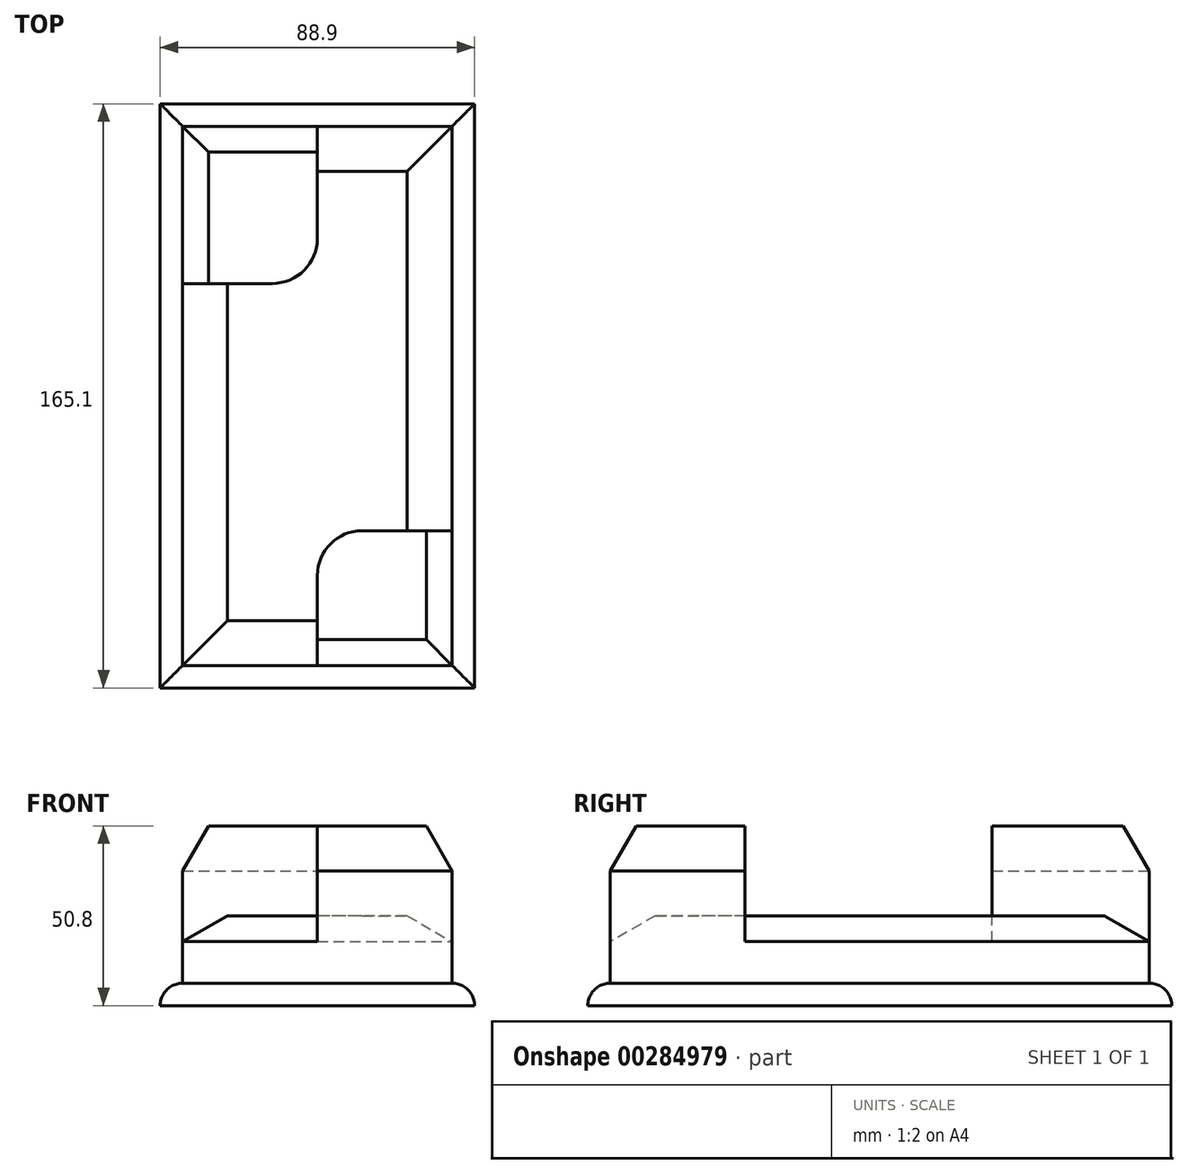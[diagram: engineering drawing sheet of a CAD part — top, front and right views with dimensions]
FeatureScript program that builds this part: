
annotation { "Feature Type Name" : "Feature", "Feature Type Description" : "" }
export const myFeature = defineFeature(function(context is Context, id is Id, definition is map)
    precondition{}
    {
        {
            var Q0;
            Q0=qCreatedBy(makeId("Top.planeOp"),FACE);
            var sketch = newSketch(context, id + "F0", { "sketchPlane" : qUnion([Q0])});
            skLineSegment(sketch, "E0.bottom", {"start": v(-67.89, 79.36) * mm, "end": v(21.01, 79.36) * mm});
            skLineSegment(sketch, "E0.top", {"start": v(-67.89, -85.74) * mm, "end": v(21.01, -85.74) * mm});
            skLineSegment(sketch, "E0.left", {"start": v(-67.89, 79.36) * mm, "end": v(-67.89, -85.74) * mm});
            skLineSegment(sketch, "E0.right", {"start": v(21.01, 79.36) * mm, "end": v(21.01, -85.74) * mm});
            skLineSegment(sketch, "E1.bottom", {"start": v(-61.54, 73) * mm, "end": v(14.66, 73) * mm});
            skLineSegment(sketch, "E1.top", {"start": v(-61.54, -79.4) * mm, "end": v(14.66, -79.4) * mm});
            skLineSegment(sketch, "E1.left", {"start": v(-61.54, 73) * mm, "end": v(-61.54, -79.4) * mm});
            skLineSegment(sketch, "E1.right", {"start": v(14.66, 73) * mm, "end": v(14.66, -79.4) * mm});
            skLineSegment(sketch, "E2", {"start": v(-23.44, -79.4) * mm, "end": v(-23.44, -54) * mm});
            skLineSegment(sketch, "E3", {"start": v(-10.74, -41.3) * mm, "end": v(14.66, -41.3) * mm});
            skPoint(sketch, "E4.visualSharp", {"position": v(-23.44, -41.3) * mm});
            skArc(sketch, "E4.filletArc", {"start": v(-10.74, -41.3) * mm, "mid": v(-19.72, -45.01) * mm, "end": v(-23.44, -54) * mm});
            skLineSegment(sketch, "E5", {"start": v(-61.54, 28.56) * mm, "end": v(-36.14, 28.56) * mm});
            skLineSegment(sketch, "E6", {"start": v(-23.44, 41.26) * mm, "end": v(-23.44, 73) * mm});
            skPoint(sketch, "E7.visualSharp", {"position": v(-23.44, 28.56) * mm});
            skArc(sketch, "E7.filletArc", {"start": v(-36.14, 28.56) * mm, "mid": v(-27.16, 32.28) * mm, "end": v(-23.44, 41.26) * mm});
            skSolve(sketch);
        }
        {
            var Q0;
            Q0=makeQuery(id+"F0.imprint","IMPRINT",FACE,{"disambiguationData":[TD([[makeQuery(id+"F0.imprint","IMPRINT",EDGE,{"derivedFrom":sQuery(id+"F0.wireOp",EDGE,"E0.bottom")}),-1.0]])]});
            extrude(context, id + "F1", {"entities" : qUnion([Q0]), "depth" : 6.35 * mm});
        }
        {
            var Q0;
            {var subQ4=sQuery(id+"F0.wireOp",EDGE,"E2");Q0=makeQuery(id+"F0.imprint","IMPRINT",FACE,{"disambiguationData":[TD([[makeQuery(id+"F0.imprint","IMPRINT",EDGE,{"derivedFrom":subQ4}),1.0]])]});}
            extrude(context, id + "F2", {"entities" : qUnion([Q0]), "operationType" : NewBodyOperationType.ADD, "depth" : 25.4 * mm});
        }
        {
            var Q0;
            {var subQ1=sQuery(id+"F0.wireOp",EDGE,"E5");Q0=makeQuery(id+"F0.imprint","IMPRINT",FACE,{"disambiguationData":[TD([[makeQuery(id+"F0.imprint","IMPRINT",EDGE,{"derivedFrom":subQ1}),1.0]])]});}
            var Q1;
            {var subQ4=sQuery(id+"F0.wireOp",EDGE,"E2");Q1=makeQuery(id+"F0.imprint","IMPRINT",FACE,{"disambiguationData":[TD([[makeQuery(id+"F0.imprint","IMPRINT",EDGE,{"derivedFrom":subQ4}),-1.0]])]});}
            extrude(context, id + "F3", {"entities" : qUnion([Q0, Q1]), "operationType" : NewBodyOperationType.ADD, "depth" : 50.8 * mm});
        }
        {
            var Q0;
            Q0=makeQuery(id+"F1.opExtrude","CAP_EDGE",EDGE,{"disambiguationData":[OSD([sQuery(id+"F0.wireOp",EDGE,"E0.bottom")])],"isStart":false});
            var Q1;
            Q1=makeQuery(id+"F1.opExtrude","CAP_EDGE",EDGE,{"disambiguationData":[OSD([sQuery(id+"F0.wireOp",EDGE,"E0.left")])],"isStart":false});
            var Q2;
            Q2=makeQuery(id+"F1.opExtrude","CAP_EDGE",EDGE,{"disambiguationData":[OSD([sQuery(id+"F0.wireOp",EDGE,"E0.top")])],"isStart":false});
            var Q3;
            Q3=makeQuery(id+"F1.opExtrude","CAP_EDGE",EDGE,{"disambiguationData":[OSD([sQuery(id+"F0.wireOp",EDGE,"E0.right")])],"isStart":false});
            fillet(context, id + "F4", {"entities" : qUnion([Q0, Q1, Q2, Q3]), "radius" : 6.35 * mm, "tangentPropagation" : true, "allowEdgeOverflow" : false});
        }
        {
            var Q0;
            Q0=makeQuery(id+"F2.opExtrude","CAP_EDGE",EDGE,{"disambiguationData":[OSD([sQuery(id+"F0.wireOp",EDGE,"E1.left")])],"isStart":false});
            var Q1;
            Q1=makeQuery(id+"F2.opExtrude","CAP_EDGE",EDGE,{"disambiguationData":[OSD([sQuery(id+"F0.wireOp",EDGE,"E1.bottom")])],"isStart":false});
            var Q2;
            Q2=makeQuery(id+"F2.opExtrude","CAP_EDGE",EDGE,{"disambiguationData":[OSD([sQuery(id+"F0.wireOp",EDGE,"E1.right")])],"isStart":false});
            var Q3;
            Q3=makeQuery(id+"F2.opExtrude","CAP_EDGE",EDGE,{"disambiguationData":[OSD([sQuery(id+"F0.wireOp",EDGE,"E1.top")])],"isStart":false});
            chamfer(context, id + "F5", {"entities" : qUnion([Q0, Q1, Q2, Q3]), "chamferType" : ChamferType.OFFSET_ANGLE, "width" : 12.7 * mm, "oppositeDirection" : false, "angle" : 30 * degree, "tangentPropagation" : true});
        }
        {
            var Q0;
            Q0=makeQuery(id+"F3.opExtrude","CAP_EDGE",EDGE,{"disambiguationData":[OSD([sQuery(id+"F0.wireOp",EDGE,"E1.bottom")])],"isStart":false});
            var Q1;
            Q1=makeQuery(id+"F3.opExtrude","CAP_EDGE",EDGE,{"disambiguationData":[OSD([sQuery(id+"F0.wireOp",EDGE,"E1.left")])],"isStart":false});
            chamfer(context, id + "F6", {"entities" : qUnion([Q0, Q1]), "chamferType" : ChamferType.OFFSET_ANGLE, "width" : 12.7 * mm, "oppositeDirection" : false, "angle" : 30 * degree, "tangentPropagation" : true});
        }
        {
            var Q0;
            Q0=makeQuery(id+"F3.opExtrude","CAP_EDGE",EDGE,{"disambiguationData":[OSD([sQuery(id+"F0.wireOp",EDGE,"E1.right")])],"isStart":false});
            var Q1;
            Q1=makeQuery(id+"F3.opExtrude","CAP_EDGE",EDGE,{"disambiguationData":[OSD([sQuery(id+"F0.wireOp",EDGE,"E1.top")])],"isStart":false});
            chamfer(context, id + "F7", {"entities" : qUnion([Q0, Q1]), "chamferType" : ChamferType.OFFSET_ANGLE, "width" : 12.7 * mm, "oppositeDirection" : false, "angle" : 30 * degree, "tangentPropagation" : true});
        }
    });
